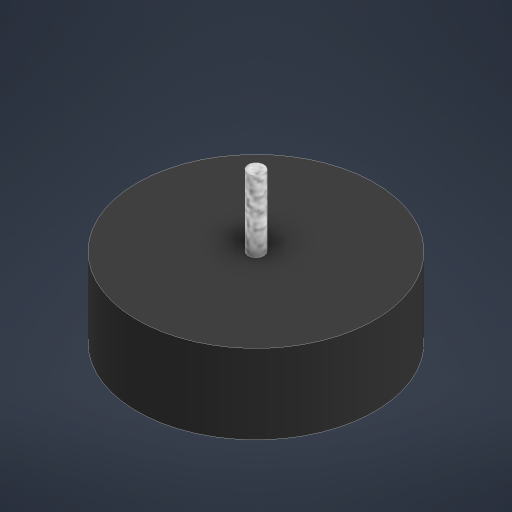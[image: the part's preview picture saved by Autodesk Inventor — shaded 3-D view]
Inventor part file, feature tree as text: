
AUTODESK INVENTOR PART (.ipt)
format: ipt  version: 2023 (Build 270158000, 158)  size: 167,424 bytes
history: native  units: mm
features: extrude x2, sketch x2, other x1
ambient origin geometry x8: Origin, YZ Plane, XZ Plane, XY Plane, X Axis, Y Axis, Z Axis, Center Point
bodies: Body1 (feature_tree)
feature tree (5):
  other  "Těleso1"
  extrude  "Vysunutí1"  Depth=30.0mm
  extrude  "Vysunutí2"  Depth=10.0mm TaperAngle=0.0deg
  sketch  "Náčrt2"
  sketch  "Náčrt3"
